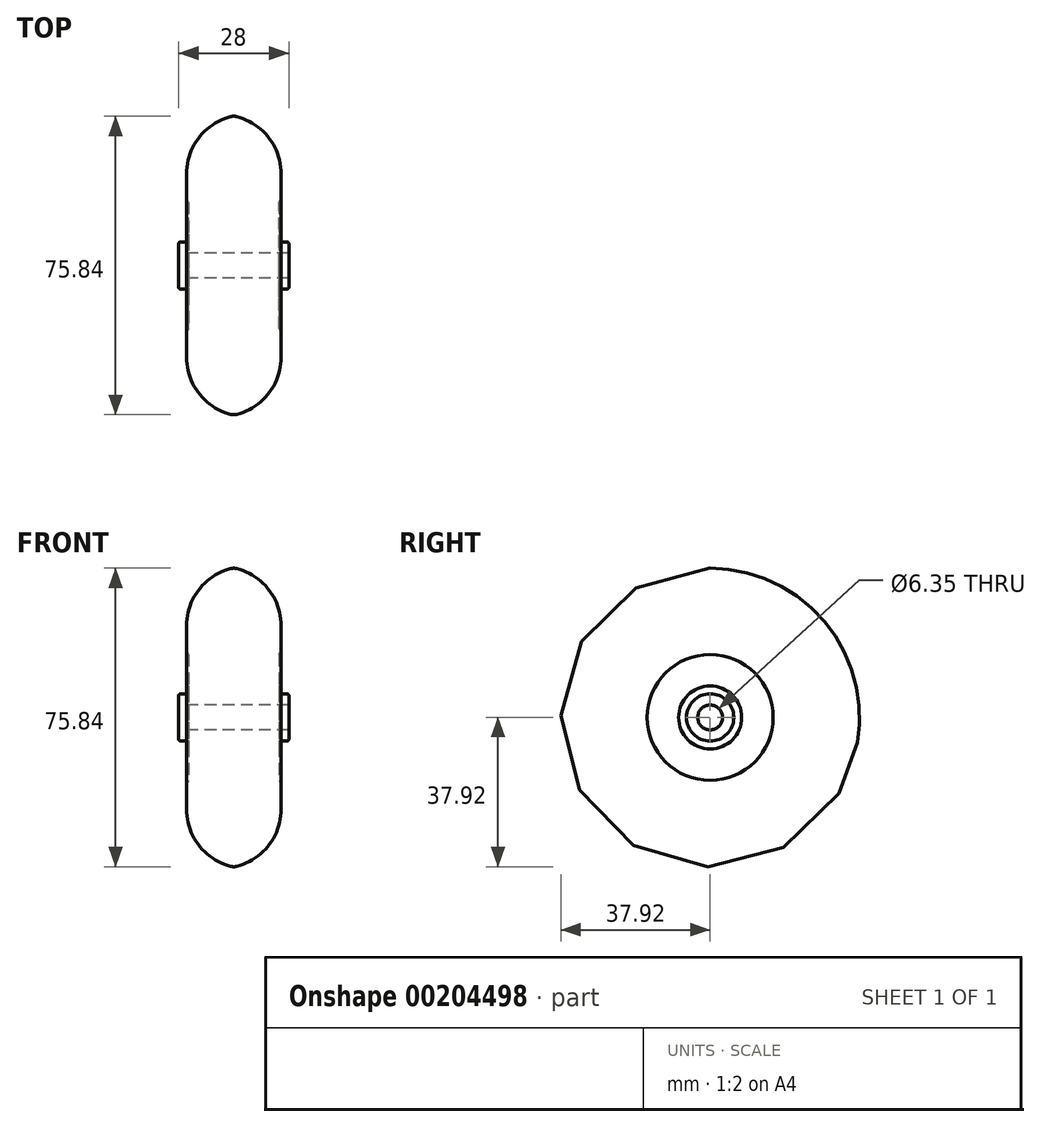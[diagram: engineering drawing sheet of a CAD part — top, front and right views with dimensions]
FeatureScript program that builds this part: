
annotation { "Feature Type Name" : "Feature", "Feature Type Description" : "" }
export const myFeature = defineFeature(function(context is Context, id is Id, definition is map)
    precondition{}
    {
        {
            var Q0;
            Q0=qCreatedBy(makeId("Front.planeOp"),FACE);
            var sketch = newSketch(context, id + "F0", { "sketchPlane" : qUnion([Q0])});
            skLineSegment(sketch, "E0", {"start": v(-13.97, 0) * mm, "end": v(13.97, 0) * mm, "construction": true});
            skPoint(sketch, "E1", {"position": v(0, 0) * mm});
            skLineSegment(sketch, "E2", {"start": v(0, 3.18) * mm, "end": v(-14, 3.18) * mm});
            skLineSegment(sketch, "E3", {"start": v(-14, 3.17) * mm, "end": v(-14, 5.5) * mm});
            skLineSegment(sketch, "E4", {"start": v(-13.5, 6) * mm, "end": v(-12, 6) * mm});
            skLineSegment(sketch, "E5", {"start": v(-12, 6) * mm, "end": v(-12, 8) * mm});
            skLineSegment(sketch, "E6", {"start": v(-12, 8) * mm, "end": v(-11.5, 8) * mm});
            skLineSegment(sketch, "E7", {"start": v(-11.5, 8) * mm, "end": v(-11.5, 16) * mm});
            skLineSegment(sketch, "E8", {"start": v(-11.5, 16) * mm, "end": v(-11.73, 16.4) * mm});
            skLineSegment(sketch, "E9", {"start": v(-12, 17.4) * mm, "end": v(-12, 23.3) * mm});
            skArc(sketch, "E10", {"start": v(0, 38) * mm, "mid": v(-8.62, 32.79) * mm, "end": v(-12, 23.3) * mm});
            skPoint(sketch, "E11.visualSharp", {"position": v(-12, 16.87) * mm});
            skArc(sketch, "E11.filletArc", {"start": v(-12, 17.4) * mm, "mid": v(-11.93, 16.88) * mm, "end": v(-11.73, 16.4) * mm});
            skLineSegment(sketch, "E12", {"start": v(0, 38) * mm, "end": v(0, 0) * mm, "construction": true});
            skPoint(sketch, "E13.visualSharp", {"position": v(-14, 6) * mm});
            skArc(sketch, "E13.filletArc", {"start": v(-13.5, 6) * mm, "mid": v(-13.85, 5.85) * mm, "end": v(-14, 5.5) * mm});
            skArc(sketch, "E14.MirrorCS", {"start": v(13.5, 6) * mm, "mid": v(13.85, 5.85) * mm, "end": v(14, 5.5) * mm});
            skLineSegment(sketch, "E15.MirrorCS", {"start": v(13.5, 6) * mm, "end": v(12, 6) * mm});
            skLineSegment(sketch, "E16.MirrorCS", {"start": v(11.5, 16) * mm, "end": v(11.73, 16.4) * mm});
            skArc(sketch, "E17.MirrorCS", {"start": v(12, 17.4) * mm, "mid": v(11.93, 16.88) * mm, "end": v(11.73, 16.4) * mm});
            skLineSegment(sketch, "E18.MirrorCS", {"start": v(14, 3.17) * mm, "end": v(14, 5.5) * mm});
            skLineSegment(sketch, "E19.MirrorCS", {"start": v(12, 6) * mm, "end": v(12, 8) * mm});
            skLineSegment(sketch, "E20.MirrorCS", {"start": v(12, 8) * mm, "end": v(11.5, 8) * mm});
            skPoint(sketch, "E21.MirrorP", {"position": v(12, 16.87) * mm});
            skLineSegment(sketch, "E22.MirrorCS", {"start": v(0, 3.18) * mm, "end": v(14, 3.17) * mm});
            skPoint(sketch, "E23.MirrorP", {"position": v(14, 6) * mm});
            skLineSegment(sketch, "E24.MirrorCS", {"start": v(11.5, 8) * mm, "end": v(11.5, 16) * mm});
            skLineSegment(sketch, "E25.MirrorCS", {"start": v(12, 17.4) * mm, "end": v(12, 23.3) * mm});
            skArc(sketch, "E26.MirrorCS", {"start": v(0, 38) * mm, "mid": v(8.62, 32.79) * mm, "end": v(12, 23.3) * mm});
            skSolve(sketch);
        }
        {
            var Q0;
            Q0 = qSketchRegion(id + "F0", true);
            var Q1;
            Q1=sQuery(id+"F0.wireOp",EDGE,"E0");
            revolve(context, id + "F1", {"entities" : qUnion([Q0]), "axis" : qUnion([Q1]), "revolveType" : RevolveType.FULL});
        }
        {
            var Q0;
            Q0=makeQuery(id+"F1.opRevolve","SWEPT_EDGE",EDGE,{"disambiguationData":[OSD([sQuery(id+"F0.wireOp",EDGE,"E10"),sQuery(id+"F0.wireOp",EDGE,"E26.MirrorCS")])]});
            fillet(context, id + "F2", {"entities" : qUnion([Q0]), "radius" : 3 * mm, "tangentPropagation" : true, "allowEdgeOverflow" : false});
        }
    });
